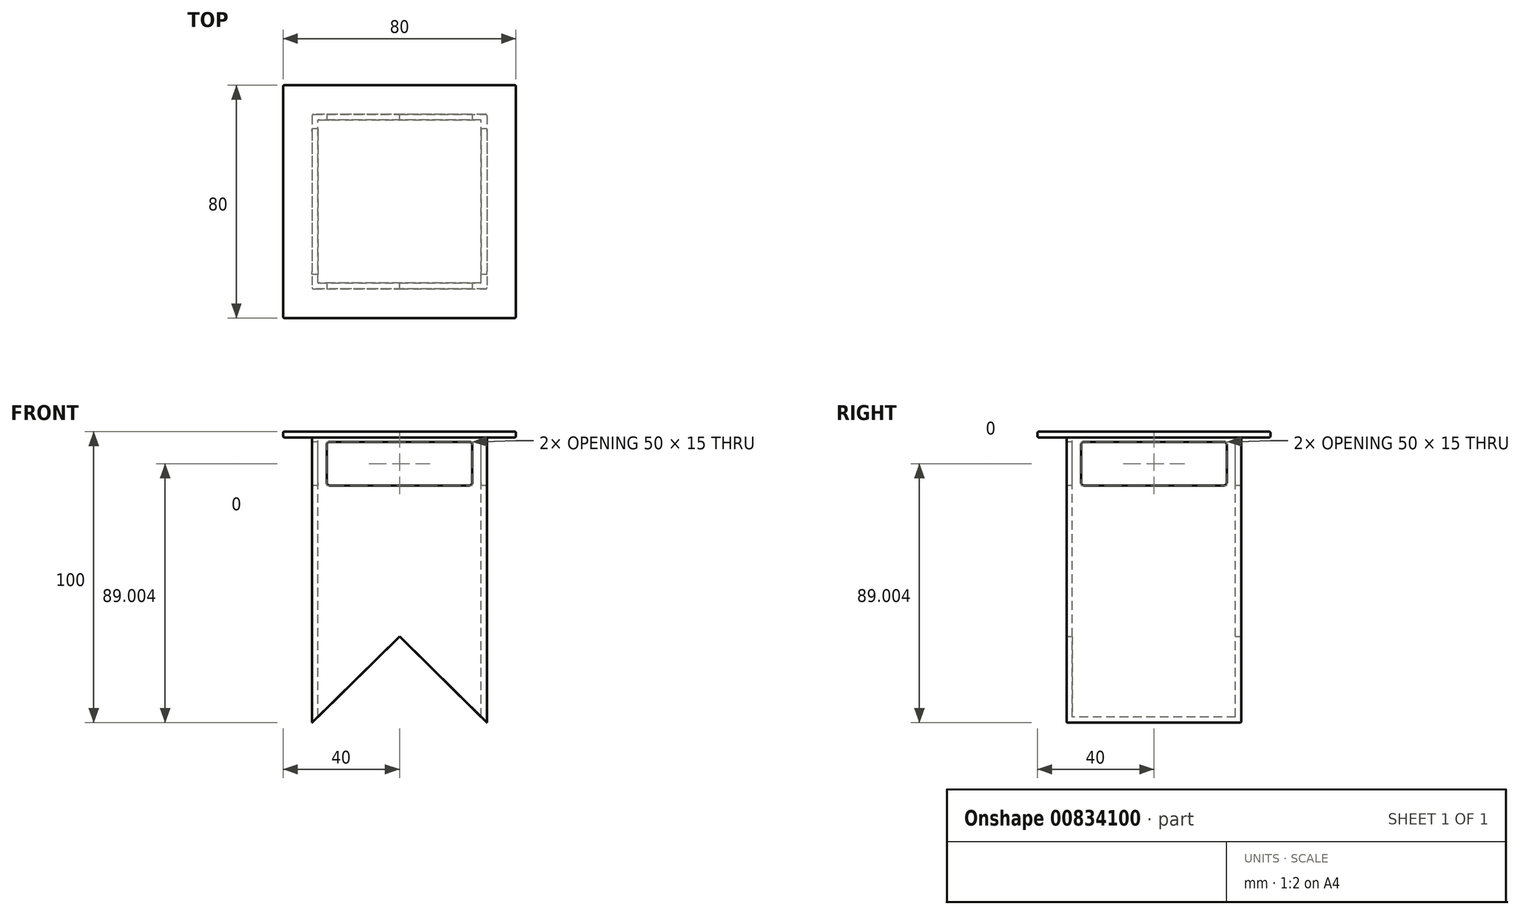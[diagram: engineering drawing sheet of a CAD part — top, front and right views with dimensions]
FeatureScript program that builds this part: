
annotation { "Feature Type Name" : "Feature", "Feature Type Description" : "" }
export const myFeature = defineFeature(function(context is Context, id is Id, definition is map)
    precondition{}
    {
        {
            var Q0;
            Q0=qCreatedBy(makeId("Front.planeOp"),FACE);
            var sketch = newSketch(context, id + "F0", { "sketchPlane" : qUnion([Q0])});
            skLineSegment(sketch, "E0", {"start": v(0, 49.22) * mm, "end": v(30, 49.22) * mm});
            skLineSegment(sketch, "E1", {"start": v(30, 49.22) * mm, "end": v(30, -50.78) * mm});
            skLineSegment(sketch, "E2", {"start": v(0, 49.22) * mm, "end": v(-30, 49.22) * mm});
            skLineSegment(sketch, "E3", {"start": v(-30, 49.22) * mm, "end": v(-30, -50.78) * mm});
            skLineSegment(sketch, "E4", {"start": v(-30, -50.78) * mm, "end": v(0, -21.08) * mm});
            skLineSegment(sketch, "E5", {"start": v(0, -21.08) * mm, "end": v(30, -50.78) * mm});
            skSolve(sketch);
        }
        {
            var Q0;
            Q0=makeQuery(id+"F0.imprint","IMPRINT",FACE,{"disambiguationData":[TD([[makeQuery(id+"F0.imprint","IMPRINT",EDGE,{"derivedFrom":sQuery(id+"F0.wireOp",EDGE,"E0")}),-1.0]])]});
            var Q1;
            Q1=sQuery(id+"F0.wireOp",EDGE,"E5");
            var Q2;
            Q2=sQuery(id+"F0.wireOp",EDGE,"E1");
            var Q3;
            Q3=sQuery(id+"F0.wireOp",EDGE,"E4");
            var Q4;
            Q4=sQuery(id+"F0.wireOp",EDGE,"E0");
            var Q5;
            Q5=sQuery(id+"F0.wireOp",EDGE,"E2");
            var Q6;
            Q6=sQuery(id+"F0.wireOp",EDGE,"E3");
            extrude(context, id + "F1", {"entities" : qUnion([Q0]), "surfaceEntities" : qUnion([Q1, Q2, Q3, Q4, Q5, Q6]), "endBound" : BoundingType.SYMMETRIC, "depth" : 60 * mm, "offsetDistance" : 25 * mm});
        }
        {
            var Q0;
            Q0=makeQuery(id+"F1.opExtrude","SWEPT_FACE",FACE,{"disambiguationData":[OSD([sQuery(id+"F0.wireOp",EDGE,"E0"),sQuery(id+"F0.wireOp",EDGE,"E2")])]});
            var sketch = newSketch(context, id + "F2", { "sketchPlane" : qUnion([Q0])});
            skLineSegment(sketch, "E6.bottom", {"start": v(-28, 28) * mm, "end": v(28, 28) * mm});
            skLineSegment(sketch, "E6.top", {"start": v(-28, -28) * mm, "end": v(28, -28) * mm});
            skLineSegment(sketch, "E6.left", {"start": v(-28, 28) * mm, "end": v(-28, -28) * mm});
            skLineSegment(sketch, "E6.right", {"start": v(28, 28) * mm, "end": v(28, -28) * mm});
            skSolve(sketch);
        }
        {
            var Q0;
            Q0=makeQuery(id+"F2.imprint","IMPRINT",FACE,{"disambiguationData":[TD([[makeQuery(id+"F2.imprint","IMPRINT",EDGE,{"derivedFrom":sQuery(id+"F2.wireOp",EDGE,"E6.bottom")}),-1.0]])]});
            extrude(context, id + "F3", {"entities" : qUnion([Q0]), "operationType" : NewBodyOperationType.REMOVE, "endBound" : BoundingType.THROUGH_ALL, "oppositeDirection" : true, "depth" : 100 * mm, "offsetDistance" : 25 * mm});
        }
        {
            var Q0;
            Q0=makeQuery(id+"F1.opExtrude","CAP_FACE",FACE,{"disambiguationData":[OSD([sQuery(id+"F0.wireOp",EDGE,"E0"),sQuery(id+"F0.wireOp",EDGE,"E1"),sQuery(id+"F0.wireOp",EDGE,"E2"),sQuery(id+"F0.wireOp",EDGE,"E3"),sQuery(id+"F0.wireOp",EDGE,"E4"),sQuery(id+"F0.wireOp",EDGE,"E5")])],"isStart":false});
            var sketch = newSketch(context, id + "F4", { "sketchPlane" : qUnion([Q0])});
            skLineSegment(sketch, "E7.bottom", {"start": v(25, 30.72) * mm, "end": v(-25, 30.72) * mm});
            skLineSegment(sketch, "E7.top", {"start": v(25, 45.72) * mm, "end": v(-25, 45.72) * mm});
            skLineSegment(sketch, "E7.left", {"start": v(25, 30.72) * mm, "end": v(25, 45.72) * mm});
            skLineSegment(sketch, "E7.right", {"start": v(-25, 30.72) * mm, "end": v(-25, 45.72) * mm});
            skPoint(sketch, "E7.middle", {"position": v(0, 38.22) * mm});
            skSolve(sketch);
        }
        {
            var Q0;
            Q0=makeQuery(id+"F4.imprint","IMPRINT",FACE,{"disambiguationData":[TD([[makeQuery(id+"F4.imprint","IMPRINT",EDGE,{"derivedFrom":sQuery(id+"F4.wireOp",EDGE,"E7.bottom")}),-1.0]])]});
            extrude(context, id + "F5", {"entities" : qUnion([Q0]), "operationType" : NewBodyOperationType.REMOVE, "oppositeDirection" : true, "depth" : 60 * mm, "offsetDistance" : 25 * mm});
        }
        {
            var Q0;
            Q0=qCreatedBy(makeId("Right.planeOp"),FACE);
            var sketch = newSketch(context, id + "F6", { "sketchPlane" : qUnion([Q0])});
            skLineSegment(sketch, "E8.bottom", {"start": v(25, 30.72) * mm, "end": v(-25, 30.72) * mm});
            skLineSegment(sketch, "E8.top", {"start": v(25, 45.72) * mm, "end": v(-25, 45.72) * mm});
            skLineSegment(sketch, "E8.left", {"start": v(25, 30.72) * mm, "end": v(25, 45.72) * mm});
            skLineSegment(sketch, "E8.right", {"start": v(-25, 30.72) * mm, "end": v(-25, 45.72) * mm});
            skPoint(sketch, "E8.middle", {"position": v(0, 38.22) * mm});
            skSolve(sketch);
        }
        {
            var Q0;
            Q0 = qSketchRegion(id + "F6", true);
            extrude(context, id + "F7", {"entities" : qUnion([Q0]), "operationType" : NewBodyOperationType.REMOVE, "endBound" : BoundingType.SYMMETRIC, "depth" : 60 * mm, "offsetDistance" : 25 * mm});
        }
        {
            var Q0;
            Q0=makeQuery(id+"F1.opExtrude","SWEPT_FACE",FACE,{"disambiguationData":[OSD([sQuery(id+"F0.wireOp",EDGE,"E0"),sQuery(id+"F0.wireOp",EDGE,"E2")])]});
            var sketch = newSketch(context, id + "F8", { "sketchPlane" : qUnion([Q0])});
            skLineSegment(sketch, "E9.bottom", {"start": v(40, 40) * mm, "end": v(-40, 40) * mm});
            skLineSegment(sketch, "E9.top", {"start": v(40, -40) * mm, "end": v(-40, -40) * mm});
            skLineSegment(sketch, "E9.left", {"start": v(40, 40) * mm, "end": v(40, -40) * mm});
            skLineSegment(sketch, "E9.right", {"start": v(-40, 40) * mm, "end": v(-40, -40) * mm});
            skPoint(sketch, "E9.middle", {"position": v(0, 0) * mm});
            skSolve(sketch);
        }
        {
            var Q0;
            Q0 = qSketchRegion(id + "F8", true);
            extrude(context, id + "F9", {"entities" : qUnion([Q0]), "operationType" : NewBodyOperationType.ADD, "depth" : -2 * mm, "offsetDistance" : 25 * mm});
        }
        {
            var Q0;
            {var subQ0=sQuery(id+"F6.wireOp",EDGE,"E8.left");var subQ1=sQuery(id+"F6.wireOp",EDGE,"E8.bottom");Q0=makeQuery(id+"F7.boolean.opBoolean","COPY",EDGE,{"disambiguationData":[TD([makeQuery(id+"F1.opExtrude","SWEPT_FACE",FACE,{"disambiguationData":[OSD([sQuery(id+"F0.wireOp",EDGE,"E3")])]})])],"derivedFrom":makeQuery(id+"F7.opExtrude","SWEPT_EDGE",EDGE,{"disambiguationData":[OSD([subQ1,subQ0])]})});}
            var Q1;
            {var subQ0=sQuery(id+"F6.wireOp",EDGE,"E8.bottom");var subQ1=sQuery(id+"F6.wireOp",EDGE,"E8.right");Q1=makeQuery(id+"F7.boolean.opBoolean","COPY",EDGE,{"disambiguationData":[TD([makeQuery(id+"F1.opExtrude","SWEPT_FACE",FACE,{"disambiguationData":[OSD([sQuery(id+"F0.wireOp",EDGE,"E3")])]})])],"derivedFrom":makeQuery(id+"F7.opExtrude","SWEPT_EDGE",EDGE,{"disambiguationData":[OSD([subQ0,subQ1])]})});}
            var Q2;
            {var subQ0=sQuery(id+"F6.wireOp",EDGE,"E8.top");var subQ1=sQuery(id+"F6.wireOp",EDGE,"E8.right");Q2=makeQuery(id+"F7.boolean.opBoolean","COPY",EDGE,{"disambiguationData":[TD([makeQuery(id+"F1.opExtrude","SWEPT_FACE",FACE,{"disambiguationData":[OSD([sQuery(id+"F0.wireOp",EDGE,"E3")])]})])],"derivedFrom":makeQuery(id+"F7.opExtrude","SWEPT_EDGE",EDGE,{"disambiguationData":[OSD([subQ0,subQ1])]})});}
            var Q3;
            {var subQ0=sQuery(id+"F6.wireOp",EDGE,"E8.left");var subQ1=sQuery(id+"F6.wireOp",EDGE,"E8.top");Q3=makeQuery(id+"F7.boolean.opBoolean","COPY",EDGE,{"disambiguationData":[TD([makeQuery(id+"F1.opExtrude","SWEPT_FACE",FACE,{"disambiguationData":[OSD([sQuery(id+"F0.wireOp",EDGE,"E3")])]})])],"derivedFrom":makeQuery(id+"F7.opExtrude","SWEPT_EDGE",EDGE,{"disambiguationData":[OSD([subQ1,subQ0])]})});}
            fillet(context, id + "F10", {"entities" : qUnion([Q0, Q1, Q2, Q3]), "radius" : 1 * mm, "tangentPropagation" : true, "allowEdgeOverflow" : false});
        }
        {
            var Q0;
            {var subQ0=sQuery(id+"F4.wireOp",EDGE,"E7.top");var subQ1=sQuery(id+"F4.wireOp",EDGE,"E7.right");Q0=makeQuery(id+"F5.boolean.opBoolean","COPY",EDGE,{"disambiguationData":[TD([makeQuery(id+"F3.boolean.opBoolean","COPY",FACE,{"derivedFrom":makeQuery(id+"F3.opExtrude","SWEPT_FACE",FACE,{"disambiguationData":[OSD([sQuery(id+"F2.wireOp",EDGE,"E6.bottom")])]})})])],"derivedFrom":makeQuery(id+"F5.opExtrude","SWEPT_EDGE",EDGE,{"disambiguationData":[OSD([subQ0,subQ1])]})});}
            var Q1;
            {var subQ0=sQuery(id+"F4.wireOp",EDGE,"E7.bottom");var subQ1=sQuery(id+"F4.wireOp",EDGE,"E7.right");Q1=makeQuery(id+"F5.boolean.opBoolean","COPY",EDGE,{"disambiguationData":[TD([makeQuery(id+"F3.boolean.opBoolean","COPY",FACE,{"derivedFrom":makeQuery(id+"F3.opExtrude","SWEPT_FACE",FACE,{"disambiguationData":[OSD([sQuery(id+"F2.wireOp",EDGE,"E6.bottom")])]})})])],"derivedFrom":makeQuery(id+"F5.opExtrude","SWEPT_EDGE",EDGE,{"disambiguationData":[OSD([subQ0,subQ1])]})});}
            var Q2;
            {var subQ0=sQuery(id+"F4.wireOp",EDGE,"E7.bottom");var subQ1=sQuery(id+"F4.wireOp",EDGE,"E7.left");Q2=makeQuery(id+"F5.boolean.opBoolean","COPY",EDGE,{"disambiguationData":[TD([makeQuery(id+"F3.boolean.opBoolean","COPY",FACE,{"derivedFrom":makeQuery(id+"F3.opExtrude","SWEPT_FACE",FACE,{"disambiguationData":[OSD([sQuery(id+"F2.wireOp",EDGE,"E6.bottom")])]})})])],"derivedFrom":makeQuery(id+"F5.opExtrude","SWEPT_EDGE",EDGE,{"disambiguationData":[OSD([subQ0,subQ1])]})});}
            var Q3;
            {var subQ0=sQuery(id+"F4.wireOp",EDGE,"E7.top");var subQ1=sQuery(id+"F4.wireOp",EDGE,"E7.left");Q3=makeQuery(id+"F5.boolean.opBoolean","COPY",EDGE,{"disambiguationData":[TD([makeQuery(id+"F3.boolean.opBoolean","COPY",FACE,{"derivedFrom":makeQuery(id+"F3.opExtrude","SWEPT_FACE",FACE,{"disambiguationData":[OSD([sQuery(id+"F2.wireOp",EDGE,"E6.bottom")])]})})])],"derivedFrom":makeQuery(id+"F5.opExtrude","SWEPT_EDGE",EDGE,{"disambiguationData":[OSD([subQ0,subQ1])]})});}
            fillet(context, id + "F11", {"entities" : qUnion([Q0, Q1, Q2, Q3]), "radius" : 1 * mm, "tangentPropagation" : true, "allowEdgeOverflow" : false});
        }
        {
            var Q0;
            {var subQ0=sQuery(id+"F6.wireOp",EDGE,"E8.top");var subQ1=sQuery(id+"F6.wireOp",EDGE,"E8.left");Q0=makeQuery(id+"F7.boolean.opBoolean","COPY",EDGE,{"disambiguationData":[TD([makeQuery(id+"F1.opExtrude","SWEPT_FACE",FACE,{"disambiguationData":[OSD([sQuery(id+"F0.wireOp",EDGE,"E1")])]})])],"derivedFrom":makeQuery(id+"F7.opExtrude","SWEPT_EDGE",EDGE,{"disambiguationData":[OSD([subQ0,subQ1])]})});}
            var Q1;
            {var subQ0=sQuery(id+"F6.wireOp",EDGE,"E8.right");var subQ1=sQuery(id+"F6.wireOp",EDGE,"E8.top");Q1=makeQuery(id+"F7.boolean.opBoolean","COPY",EDGE,{"disambiguationData":[TD([makeQuery(id+"F1.opExtrude","SWEPT_FACE",FACE,{"disambiguationData":[OSD([sQuery(id+"F0.wireOp",EDGE,"E1")])]})])],"derivedFrom":makeQuery(id+"F7.opExtrude","SWEPT_EDGE",EDGE,{"disambiguationData":[OSD([subQ1,subQ0])]})});}
            var Q2;
            {var subQ0=sQuery(id+"F6.wireOp",EDGE,"E8.bottom");var subQ1=sQuery(id+"F6.wireOp",EDGE,"E8.right");Q2=makeQuery(id+"F7.boolean.opBoolean","COPY",EDGE,{"disambiguationData":[TD([makeQuery(id+"F1.opExtrude","SWEPT_FACE",FACE,{"disambiguationData":[OSD([sQuery(id+"F0.wireOp",EDGE,"E1")])]})])],"derivedFrom":makeQuery(id+"F7.opExtrude","SWEPT_EDGE",EDGE,{"disambiguationData":[OSD([subQ0,subQ1])]})});}
            var Q3;
            {var subQ0=sQuery(id+"F6.wireOp",EDGE,"E8.bottom");var subQ1=sQuery(id+"F6.wireOp",EDGE,"E8.left");Q3=makeQuery(id+"F7.boolean.opBoolean","COPY",EDGE,{"disambiguationData":[TD([makeQuery(id+"F1.opExtrude","SWEPT_FACE",FACE,{"disambiguationData":[OSD([sQuery(id+"F0.wireOp",EDGE,"E1")])]})])],"derivedFrom":makeQuery(id+"F7.opExtrude","SWEPT_EDGE",EDGE,{"disambiguationData":[OSD([subQ0,subQ1])]})});}
            fillet(context, id + "F12", {"entities" : qUnion([Q0, Q1, Q2, Q3]), "radius" : 1 * mm, "tangentPropagation" : true, "allowEdgeOverflow" : false});
        }
        {
            var Q0;
            {var subQ0=sQuery(id+"F4.wireOp",EDGE,"E7.bottom");var subQ1=sQuery(id+"F4.wireOp",EDGE,"E7.left");Q0=makeQuery(id+"F5.boolean.opBoolean","COPY",EDGE,{"disambiguationData":[TD([makeQuery(id+"F3.boolean.opBoolean","COPY",FACE,{"derivedFrom":makeQuery(id+"F3.opExtrude","SWEPT_FACE",FACE,{"disambiguationData":[OSD([sQuery(id+"F2.wireOp",EDGE,"E6.top")])]})})])],"derivedFrom":makeQuery(id+"F5.opExtrude","SWEPT_EDGE",EDGE,{"disambiguationData":[OSD([subQ0,subQ1])]})});}
            var Q1;
            {var subQ0=sQuery(id+"F4.wireOp",EDGE,"E7.top");var subQ1=sQuery(id+"F4.wireOp",EDGE,"E7.left");Q1=makeQuery(id+"F5.boolean.opBoolean","COPY",EDGE,{"disambiguationData":[TD([makeQuery(id+"F3.boolean.opBoolean","COPY",FACE,{"derivedFrom":makeQuery(id+"F3.opExtrude","SWEPT_FACE",FACE,{"disambiguationData":[OSD([sQuery(id+"F2.wireOp",EDGE,"E6.top")])]})})])],"derivedFrom":makeQuery(id+"F5.opExtrude","SWEPT_EDGE",EDGE,{"disambiguationData":[OSD([subQ0,subQ1])]})});}
            var Q2;
            {var subQ0=sQuery(id+"F4.wireOp",EDGE,"E7.top");var subQ1=sQuery(id+"F4.wireOp",EDGE,"E7.right");Q2=makeQuery(id+"F5.boolean.opBoolean","COPY",EDGE,{"disambiguationData":[TD([makeQuery(id+"F3.boolean.opBoolean","COPY",FACE,{"derivedFrom":makeQuery(id+"F3.opExtrude","SWEPT_FACE",FACE,{"disambiguationData":[OSD([sQuery(id+"F2.wireOp",EDGE,"E6.top")])]})})])],"derivedFrom":makeQuery(id+"F5.opExtrude","SWEPT_EDGE",EDGE,{"disambiguationData":[OSD([subQ0,subQ1])]})});}
            var Q3;
            {var subQ0=sQuery(id+"F4.wireOp",EDGE,"E7.bottom");var subQ1=sQuery(id+"F4.wireOp",EDGE,"E7.right");Q3=makeQuery(id+"F5.boolean.opBoolean","COPY",EDGE,{"disambiguationData":[TD([makeQuery(id+"F3.boolean.opBoolean","COPY",FACE,{"derivedFrom":makeQuery(id+"F3.opExtrude","SWEPT_FACE",FACE,{"disambiguationData":[OSD([sQuery(id+"F2.wireOp",EDGE,"E6.top")])]})})])],"derivedFrom":makeQuery(id+"F5.opExtrude","SWEPT_EDGE",EDGE,{"disambiguationData":[OSD([subQ0,subQ1])]})});}
            fillet(context, id + "F13", {"entities" : qUnion([Q0, Q1, Q2, Q3]), "radius" : 1 * mm, "tangentPropagation" : true, "allowEdgeOverflow" : false});
        }
        {
            var Q0;
            Q0=makeQuery(id+"F1.opExtrude","CAP_EDGE",EDGE,{"disambiguationData":[OSD([sQuery(id+"F0.wireOp",EDGE,"E1")])],"isStart":true});
            var Q1;
            Q1=makeQuery(id+"F1.opExtrude","CAP_EDGE",EDGE,{"disambiguationData":[OSD([sQuery(id+"F0.wireOp",EDGE,"E1")])],"isStart":false});
            var Q2;
            Q2=makeQuery(id+"F1.opExtrude","CAP_EDGE",EDGE,{"disambiguationData":[OSD([sQuery(id+"F0.wireOp",EDGE,"E3")])],"isStart":true});
            var Q3;
            Q3=makeQuery(id+"F1.opExtrude","CAP_EDGE",EDGE,{"disambiguationData":[OSD([sQuery(id+"F0.wireOp",EDGE,"E3")])],"isStart":false});
            fillet(context, id + "F14", {"entities" : qUnion([Q0, Q1, Q2, Q3]), "radius" : 0.5 * mm, "tangentPropagation" : true, "allowEdgeOverflow" : false});
        }
        {
            var Q0;
            Q0=makeQuery(id+"F9.opExtrude","SWEPT_EDGE",EDGE,{"disambiguationData":[OSD([sQuery(id+"F8.wireOp",EDGE,"E9.top"),sQuery(id+"F8.wireOp",EDGE,"E9.left")])]});
            var Q1;
            Q1=makeQuery(id+"F9.opExtrude","CAP_EDGE",EDGE,{"disambiguationData":[OSD([sQuery(id+"F8.wireOp",EDGE,"E9.left")])],"isStart":true});
            var Q2;
            Q2=makeQuery(id+"F9.opExtrude","CAP_EDGE",EDGE,{"disambiguationData":[OSD([sQuery(id+"F8.wireOp",EDGE,"E9.left")])],"isStart":false});
            var Q3;
            Q3=makeQuery(id+"F9.opExtrude","CAP_EDGE",EDGE,{"disambiguationData":[OSD([sQuery(id+"F8.wireOp",EDGE,"E9.top")])],"isStart":false});
            var Q4;
            Q4=makeQuery(id+"F9.opExtrude","CAP_EDGE",EDGE,{"disambiguationData":[OSD([sQuery(id+"F8.wireOp",EDGE,"E9.top")])],"isStart":true});
            var Q5;
            Q5=makeQuery(id+"F9.opExtrude","SWEPT_EDGE",EDGE,{"disambiguationData":[OSD([sQuery(id+"F8.wireOp",EDGE,"E9.top"),sQuery(id+"F8.wireOp",EDGE,"E9.right")])]});
            var Q6;
            Q6=makeQuery(id+"F9.opExtrude","CAP_EDGE",EDGE,{"disambiguationData":[OSD([sQuery(id+"F8.wireOp",EDGE,"E9.right")])],"isStart":false});
            var Q7;
            Q7=makeQuery(id+"F9.opExtrude","CAP_EDGE",EDGE,{"disambiguationData":[OSD([sQuery(id+"F8.wireOp",EDGE,"E9.right")])],"isStart":true});
            var Q8;
            Q8=makeQuery(id+"F9.opExtrude","CAP_EDGE",EDGE,{"disambiguationData":[OSD([sQuery(id+"F8.wireOp",EDGE,"E9.bottom")])],"isStart":false});
            var Q9;
            Q9=makeQuery(id+"F9.opExtrude","CAP_EDGE",EDGE,{"disambiguationData":[OSD([sQuery(id+"F8.wireOp",EDGE,"E9.bottom")])],"isStart":true});
            var Q10;
            Q10=makeQuery(id+"F9.opExtrude","SWEPT_EDGE",EDGE,{"disambiguationData":[OSD([sQuery(id+"F8.wireOp",EDGE,"E9.bottom"),sQuery(id+"F8.wireOp",EDGE,"E9.right")])]});
            var Q11;
            Q11=makeQuery(id+"F9.opExtrude","SWEPT_EDGE",EDGE,{"disambiguationData":[OSD([sQuery(id+"F8.wireOp",EDGE,"E9.bottom"),sQuery(id+"F8.wireOp",EDGE,"E9.left")])]});
            fillet(context, id + "F15", {"entities" : qUnion([Q0, Q1, Q2, Q3, Q4, Q5, Q6, Q7, Q8, Q9, Q10, Q11]), "radius" : 0.5 * mm, "tangentPropagation" : true, "allowEdgeOverflow" : false});
        }
        {
            var Q0;
            Q0=makeQuery(id+"F9.boolean.opBoolean","INTERSECT",EDGE,{"derivedFrom":[makeQuery(id+"F1.opExtrude","CAP_FACE",FACE,{"disambiguationData":[OSD([sQuery(id+"F0.wireOp",EDGE,"E0"),sQuery(id+"F0.wireOp",EDGE,"E1"),sQuery(id+"F0.wireOp",EDGE,"E2"),sQuery(id+"F0.wireOp",EDGE,"E3"),sQuery(id+"F0.wireOp",EDGE,"E4"),sQuery(id+"F0.wireOp",EDGE,"E5")])],"isStart":true}),makeQuery(id+"F9.opExtrude","CAP_FACE",FACE,{"disambiguationData":[OSD([sQuery(id+"F8.wireOp",EDGE,"E9.bottom"),sQuery(id+"F8.wireOp",EDGE,"E9.top"),sQuery(id+"F8.wireOp",EDGE,"E9.left"),sQuery(id+"F8.wireOp",EDGE,"E9.right")])],"isStart":false})]});
            fillet(context, id + "F16", {"entities" : qUnion([Q0]), "radius" : 0.5 * mm, "tangentPropagation" : true, "allowEdgeOverflow" : false});
        }
    });
